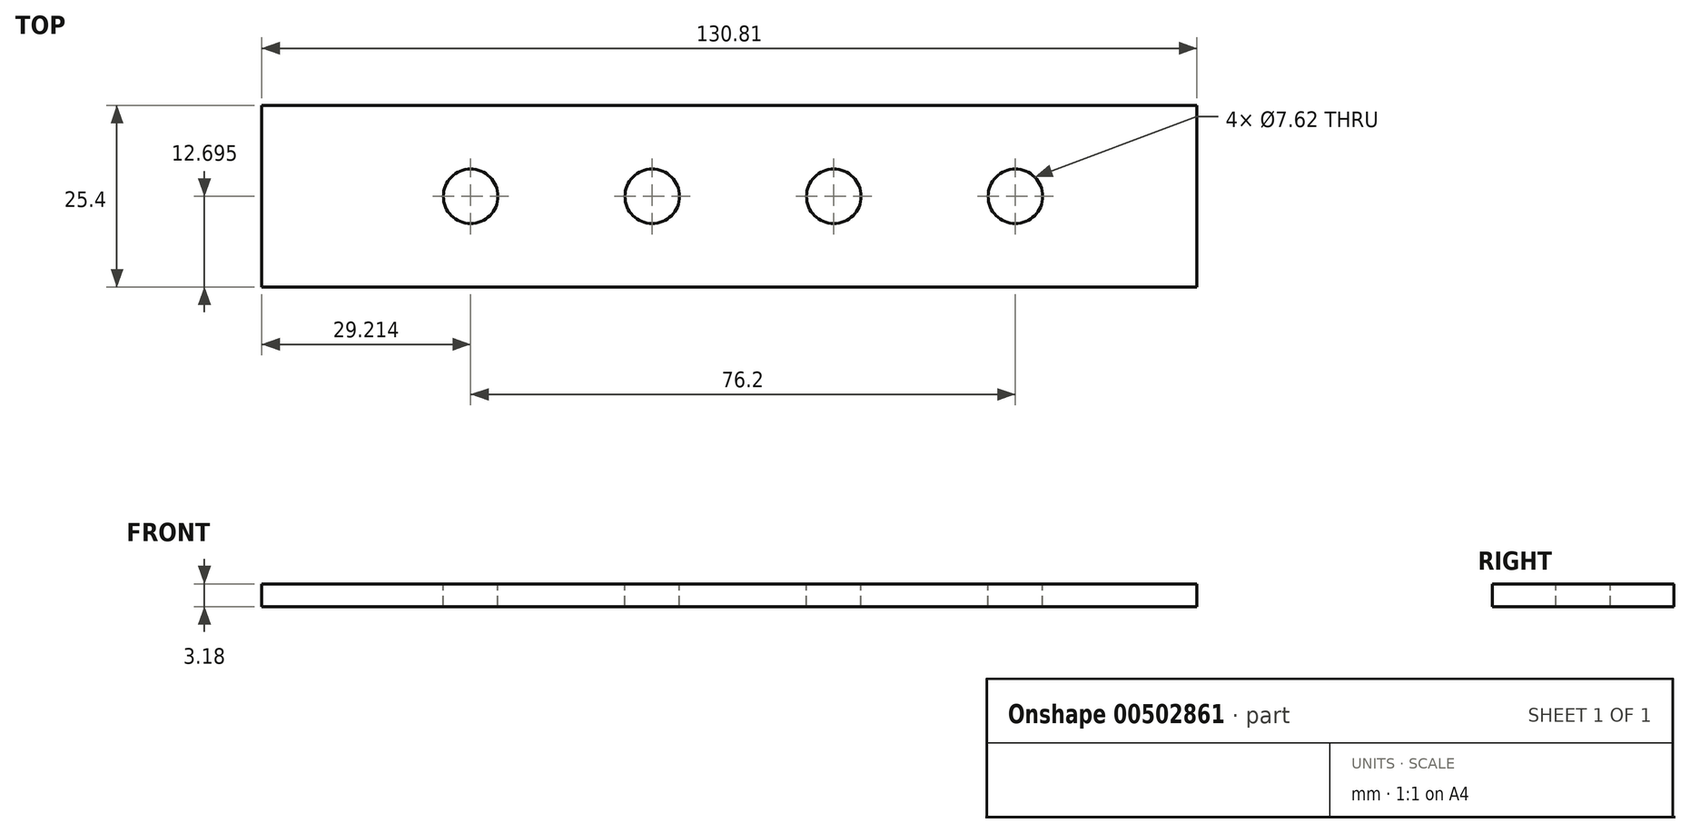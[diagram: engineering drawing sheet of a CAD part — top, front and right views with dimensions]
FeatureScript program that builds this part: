
annotation { "Feature Type Name" : "Feature", "Feature Type Description" : "" }
export const myFeature = defineFeature(function(context is Context, id is Id, definition is map)
    precondition{}
    {
        {
            var Q0;
            Q0=qCreatedBy(makeId("Top.planeOp"),FACE);
            var sketch = newSketch(context, id + "F0", { "sketchPlane" : qUnion([Q0])});
            skLineSegment(sketch, "E0.bottom", {"start": v(-40.36, 15.46) * mm, "end": v(90.45, 15.46) * mm});
            skLineSegment(sketch, "E0.top", {"start": v(-40.36, -9.94) * mm, "end": v(90.45, -9.94) * mm});
            skLineSegment(sketch, "E0.left", {"start": v(-40.36, 15.46) * mm, "end": v(-40.36, -9.94) * mm});
            skLineSegment(sketch, "E0.right", {"start": v(90.45, 15.46) * mm, "end": v(90.45, -9.94) * mm});
            skSolve(sketch);
        }
        {
            var Q0;
            Q0 = qSketchRegion(id + "F0", true);
            extrude(context, id + "F1", {"entities" : qUnion([Q0]), "depth" : 3.17 * mm});
        }
        {
            var Q0;
            Q0=makeQuery(id+"F1.opExtrude","CAP_FACE",FACE,{"disambiguationData":[OSD([sQuery(id+"F0.wireOp",EDGE,"E0.bottom"),sQuery(id+"F0.wireOp",EDGE,"E0.top"),sQuery(id+"F0.wireOp",EDGE,"E0.left"),sQuery(id+"F0.wireOp",EDGE,"E0.right")])],"isStart":false});
            var sketch = newSketch(context, id + "F2", { "sketchPlane" : qUnion([Q0])});
            skCircle(sketch, "E1", {"center": v(-11.15, 2.76) * mm, "radius": 3.81 * mm});
            skPoint(sketch, "E1.centerSnap0", {"position": v(-40.36, 2.76) * mm});
            skCircle(sketch, "E2", {"center": v(65.05, 2.76) * mm, "radius": 3.81 * mm});
            skPoint(sketch, "E2.centerSnap0", {"position": v(90.45, 2.76) * mm});
            skCircle(sketch, "E3", {"center": v(14.25, 2.76) * mm, "radius": 3.81 * mm});
            skCircle(sketch, "E4", {"center": v(39.65, 2.76) * mm, "radius": 3.81 * mm});
            skSolve(sketch);
        }
        {
            var Q0;
            Q0 = qSketchRegion(id + "F2", true);
            extrude(context, id + "F3", {"entities" : qUnion([Q0]), "operationType" : NewBodyOperationType.REMOVE, "oppositeDirection" : true, "depth" : 25.4 * mm});
        }
    });
